# Revit family: Zumtobel PANOS - INF R
name_source: partatom
category: Lighting Fixtures
revit_build: Autodesk Revit 2014 (Build: 20130308_1515(x64)
units: mm (PartAtom-declared; Revit-internal decimal feet)

## types (8) — shared parameters
Assembly Code = D5020200
Body = Zumtobel_Metal_White
Color Filter = 16777215
Description = LED ceiling-recessed luminaire
Dimming Lamp Color Temperature Shift = <None>
Emit Shape Visible in Rendering = Yes
Lamp = LED
Manufacturer = Zumtobel Lighting
Reflector = Zumtobel_Metal_White_Self_Illumination
Tilt Angle = -90.00°
URL = http://www.zumtobel.com
Voltage = 230 V
zero-valued in all types: Default Elevation

## per-type parameters (varying)
| type | Apparent Load | Back Height | Body Radius | Emit from Circle Diameter | Height | Length | Model | Opening Cut Radius | Opening Diameter | Opening Height | Opening Radius | Photometric Web File | Width |
| PANOS INF R100H 10W LED | 10 VA | 45 mm | 47 mm | 113 mm  [stored 0.370735 ft] | 123 mm  [stored 0.403543 ft] | 113 mm  [stored 0.370735 ft] | 60815385 | 52 mm | 78 mm  [stored 0.255906 ft] | 133 mm  [stored 0.436352 ft] | 57 mm | ST7652.IES | 113 mm  [stored 0.370735 ft] |
| PANOS INF R100H 16W LED | 10 VA | 45 mm | 47 mm | 113 mm  [stored 0.370735 ft] | 123 mm  [stored 0.403543 ft] | 113 mm  [stored 0.370735 ft] | 60815385 | 52 mm | 78 mm  [stored 0.255906 ft] | 133 mm  [stored 0.436352 ft] | 57 mm | ST7673.IES | 113 mm  [stored 0.370735 ft] |
| PANOS INF R100L 10W LED | 10 VA | 45 mm | 47 mm | 113 mm  [stored 0.370735 ft] | 93 mm  [stored 0.305118 ft] | 113 mm  [stored 0.370735 ft] | 60815376 | 52 mm | 78 mm  [stored 0.255906 ft] | 103 mm  [stored 0.337927 ft] | 57 mm | ST7640.IES | 113 mm  [stored 0.370735 ft] |
| PANOS INF R100L 16W LED | 16 VA | 45 mm | 47 mm | 113 mm  [stored 0.370735 ft] | 93 mm  [stored 0.305118 ft] | 113 mm  [stored 0.370735 ft] | 60815412 | 52 mm | 78 mm  [stored 0.255906 ft] | 103 mm  [stored 0.337927 ft] | 57 mm | ST7664.IES | 113 mm  [stored 0.370735 ft] |
| PANOS INF R150L 10W LED | 10 VA | 30 mm  [stored 0.0984252 ft] | 74 mm  [stored 0.242782 ft] | 168 mm  [stored 0.551181 ft] | 84 mm  [stored 0.275591 ft] | 168 mm  [stored 0.551181 ft] | 60815829 | 79 mm | 131 mm  [stored 0.42979 ft] | 94 mm  [stored 0.308399 ft] | 84 mm  [stored 0.275591 ft] | 60815861_(STD).IES | 168 mm  [stored 0.551181 ft] |
| PANOS INF R150H 10W LED | 10 VA | 30 mm  [stored 0.0984252 ft] | 74 mm  [stored 0.242782 ft] | 168 mm  [stored 0.551181 ft] | 106 mm  [stored 0.347769 ft] | 168 mm  [stored 0.551181 ft] | 60815837 | 79 mm | 131 mm  [stored 0.42979 ft] | 116 mm | 84 mm  [stored 0.275591 ft] | 60815837_(STD).IES | 168 mm  [stored 0.551181 ft] |
| PANOS INF R200L 16W LED | 16 VA | 30 mm  [stored 0.0984252 ft] | 99 mm | 218 mm  [stored 0.715223 ft] | 84 mm  [stored 0.275591 ft] | 218 mm  [stored 0.715223 ft] | 60815861 | 104 mm | 181 mm | 94 mm  [stored 0.308399 ft] | 109 mm  [stored 0.357612 ft] | 60815861_(STD).IES | 218 mm  [stored 0.715223 ft] |
| PANOS INF R200H 16W LED | 16 VA | 30 mm  [stored 0.0984252 ft] | 99 mm | 218 mm  [stored 0.715223 ft] | 122 mm  [stored 0.400262 ft] | 218 mm  [stored 0.715223 ft] | 60815869 | 104 mm | 181 mm | 132 mm | 109 mm  [stored 0.357612 ft] | 60815869_(STD).IES | 218 mm  [stored 0.715223 ft] |

note: [stored X ft] marks values corroborated as IEEE doubles in the binary element streams (Revit-internal decimal feet)

## geometry (parser evidence)
native form markers: Sweep x2
no freeform markers — native parametric forms only
